FCSTD DOCUMENT  (FreeCAD 0.14R3691 (Git))
Label: BaseModel-2-SketchesOnly
License: CC-BY 3.0
LicenseURL: http://creativecommons.org/licenses/by/3.0/
objects: Sketcher::SketchObject×5
note: 5 computed .brp shape members not serialized (recipe doc carries the construction recipe); baked Part::Feature solids carry a one-line shape summary decoded from their .brp

FEATURE [Sketcher::SketchObject] Sketch  label="Main"
  sketch-geometry (1):
    g0: Circle CenterX=0 CenterY=0 CenterZ=0 NormalX=0 NormalY=0 NormalZ=1 Radius=30
  constraints (2):
    c: Coincident(g0,g-1)
    c: Radius(g0) = 30
FEATURE [Sketcher::SketchObject] Sketch001  label="Reset"
  sketch-geometry (4):
    g0: LineSegment StartX=-15 StartY=-15 StartZ=0 EndX=-5 EndY=-15 EndZ=0
    g1: LineSegment StartX=-5 StartY=-15 StartZ=0 EndX=-5 EndY=-23 EndZ=0
    g2: LineSegment StartX=-5 StartY=-23 StartZ=0 EndX=-15 EndY=-23 EndZ=0
    g3: LineSegment StartX=-15 StartY=-23 StartZ=0 EndX=-15 EndY=-15 EndZ=0
  constraints (12):
    c: Coincident(g0,g1)
    c: Coincident(g1,g2)
    c: Coincident(g2,g3)
    c: Coincident(g3,g0)
    c: Horizontal(g0)
    c: Horizontal(g2)
    c: Vertical(g1)
    c: Vertical(g3)
    c: DistanceX(g2) = -10
    c: DistanceY(g1) = -8
    c: DistanceY(g-1,g0) = -15
    c: DistanceX(g-2,g0) = -5
FEATURE [Sketcher::SketchObject] Sketch002  label="Momentary"
  sketch-geometry (1):
    g0: Circle CenterX=-12 CenterY=-7 CenterZ=0 NormalX=0 NormalY=0 NormalZ=1 Radius=7.5
  constraints (3):
    c: Radius(g0) = 7.5
    c: DistanceX(g-2,g0) = -12
    c: DistanceY(g-1,g0) = -7
FEATURE [Sketcher::SketchObject] Sketch003  label="Power"
  sketch-geometry (8):
    g0: LineSegment StartX=3.33848 StartY=-1 StartZ=0 EndX=13.7801 EndY=-1 EndZ=0
    g1: LineSegment StartX=15.5 StartY=-2.7199 StartZ=0 EndX=15.5 EndY=-12.4048 EndZ=0
    g2: LineSegment StartX=13.9048 StartY=-14 StartZ=0 EndX=3.07848 EndY=-14 EndZ=0
    g3: LineSegment StartX=1.5 StartY=-12.4215 StartZ=0 EndX=1.5 EndY=-2.83848 EndZ=0
    g4: ArcOfCircle CenterX=3.33848 CenterY=-2.83848 CenterZ=0 NormalX=0 NormalY=0 NormalZ=1 Radius=1.83848 StartAngle=1.5708 EndAngle=3.14159
    g5: ArcOfCircle CenterX=13.7801 CenterY=-2.7199 CenterZ=0 NormalX=0 NormalY=0 NormalZ=1 Radius=1.7199 StartAngle=0 EndAngle=1.5708
    g6: ArcOfCircle CenterX=13.9048 CenterY=-12.4048 CenterZ=0 NormalX=0 NormalY=0 NormalZ=1 Radius=1.59525 StartAngle=4.71239 EndAngle=6.28319
    g7: ArcOfCircle CenterX=3.07848 CenterY=-12.4215 CenterZ=0 NormalX=0 NormalY=0 NormalZ=1 Radius=1.57848 StartAngle=3.14159 EndAngle=4.71239
  constraints (12):
    c: Horizontal(g0)
    c: Horizontal(g2)
    c: Vertical(g1)
    c: Vertical(g3)
    c: Tangent(g0,g4)
    c: Tangent(g3,g4)
    c: Tangent(g0,g5)
    c: Tangent(g1,g5)
    c: Tangent(g1,g6)
    c: Tangent(g2,g6)
    c: Tangent(g2,g7)
    c: Tangent(g3,g7)
FEATURE [Sketcher::SketchObject] Sketch004
  sketch-geometry (8):
    g0: LineSegment StartX=-2.3 StartY=-16 StartZ=0 EndX=2.3 EndY=-16 EndZ=0
    g1: LineSegment StartX=2.3 StartY=-16 StartZ=0 EndX=2.3 EndY=-25.1 EndZ=0
    g2: LineSegment StartX=2.3 StartY=-25.1 StartZ=0 EndX=-2.3 EndY=-25.1 EndZ=0
    g3: LineSegment StartX=-2.3 StartY=-25.1 StartZ=0 EndX=-2.3 EndY=-16 EndZ=0
    g4: LineSegment StartX=13.4 StartY=-20.6 StartZ=0 EndX=4.3 EndY=-20.6 EndZ=0
    g5: LineSegment StartX=4.3 StartY=-20.6 StartZ=0 EndX=4.3 EndY=-16 EndZ=0
    g6: LineSegment StartX=4.3 StartY=-16 StartZ=0 EndX=13.4 EndY=-16 EndZ=0
    g7: LineSegment StartX=13.4 StartY=-16 StartZ=0 EndX=13.4 EndY=-20.6 EndZ=0
  constraints (24):
    c: Coincident(g0,g1)
    c: Coincident(g1,g2)
    c: Coincident(g2,g3)
    c: Coincident(g3,g0)
    c: Horizontal(g0)
    c: Horizontal(g2)
    c: Vertical(g1)
    c: Vertical(g3)
    c: DistanceX(g0) = 4.6
    c: DistanceY(g1) = -9.1
    c: Symmetric(g0,g0,g-2)
    c: DistanceY(g-1,g0) = -16
    c: Coincident(g4,g5)
    c: Coincident(g5,g6)
    c: Coincident(g6,g7)
    c: Coincident(g7,g4)
    c: Horizontal(g4)
    c: Horizontal(g6)
    c: Vertical(g5)
    c: Vertical(g7)
    c: Equal(g5,g2)
    c: Equal(g6,g3)
    c: Distance(g5,g0) = 2
    c: DistanceY(g-1,g5) = -16
